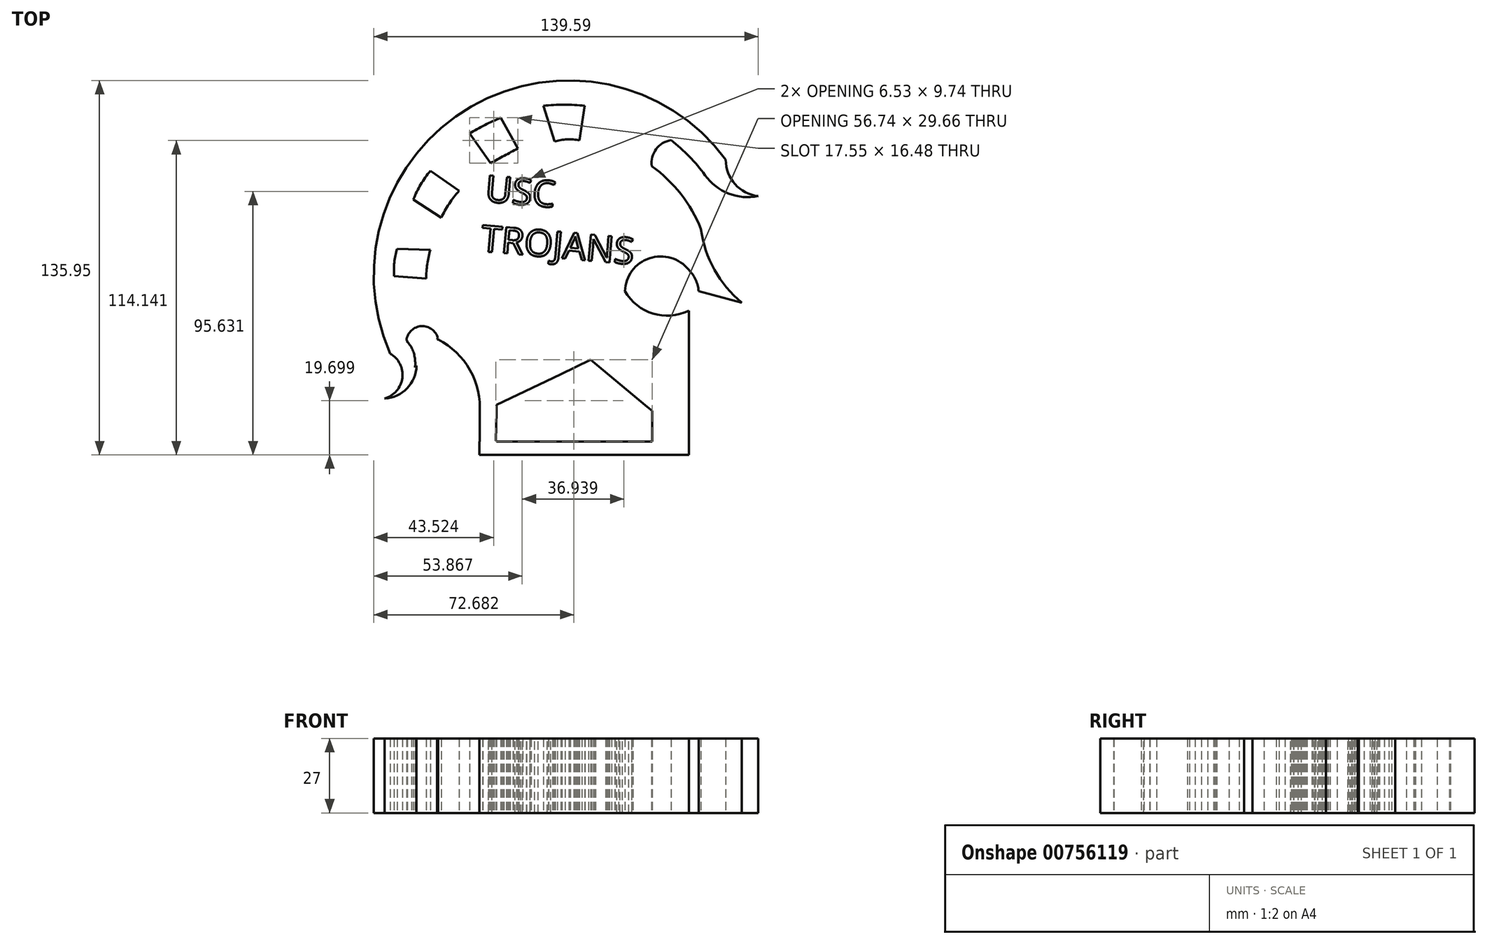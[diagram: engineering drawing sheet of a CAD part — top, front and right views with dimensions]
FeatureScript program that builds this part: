
annotation { "Feature Type Name" : "Feature", "Feature Type Description" : "" }
export const myFeature = defineFeature(function(context is Context, id is Id, definition is map)
    precondition{}
    {
        {
            var Q0;
            Q0=qCreatedBy(makeId("Top.planeOp"),FACE);
            var sketch = newSketch(context, id + "F0", { "sketchPlane" : qUnion([Q0])});
            skLineSegment(sketch, "E0", {"start": v(13.07, -40.22) * mm, "end": v(48.67, -69.88) * mm});
            skLineSegment(sketch, "E1", {"start": v(48.67, -69.88) * mm, "end": v(48.67, -22.42) * mm});
            skArc(sketch, "E2", {"start": v(25.5, -15.31) * mm, "mid": v(35.68, -23.46) * mm, "end": v(48.67, -22.42) * mm});
            skArc(sketch, "E3", {"start": v(48.67, -7.6) * mm, "mid": v(34.4, -3.36) * mm, "end": v(25.5, -15.31) * mm});
            skArc(sketch, "E4", {"start": v(52.23, -15.3) * mm, "mid": v(51.15, -11.12) * mm, "end": v(48.67, -7.6) * mm});
            skLineSegment(sketch, "E5", {"start": v(52.23, -15.3) * mm, "end": v(67.95, -19.46) * mm});
            skLineSegment(sketch, "E6", {"start": v(13.07, -40.22) * mm, "end": v(-27.27, -59.8) * mm});
            skArc(sketch, "E7", {"start": v(-27.27, -59.8) * mm, "mid": v(-30.74, -44) * mm, "end": v(-42.4, -32.8) * mm});
            skArc(sketch, "E8", {"start": v(53.1, 7.23) * mm, "mid": v(57.98, -7.53) * mm, "end": v(67.95, -19.46) * mm});
            skArc(sketch, "E9", {"start": v(53.1, 7.23) * mm, "mid": v(-15, 35.76) * mm, "end": v(-42.4, -32.8) * mm});
            skLineSegment(sketch, "E10", {"start": v(-53.77, -33.5) * mm, "end": v(-59.73, -38) * mm});
            skArc(sketch, "E11", {"start": v(-61.7, -54.3) * mm, "mid": v(-55.32, -46.8) * mm, "end": v(-59.73, -38) * mm});
            skArc(sketch, "E12", {"start": v(-61.7, -54.3) * mm, "mid": v(-50.96, -46.48) * mm, "end": v(-53.77, -33.5) * mm});
            skArc(sketch, "E13", {"start": v(54.63, 26.77) * mm, "mid": v(-26.23, 44.58) * mm, "end": v(-53.77, -33.5) * mm});
            skLineSegment(sketch, "E14", {"start": v(54.63, 26.77) * mm, "end": v(62.1, 32.38) * mm});
            skArc(sketch, "E15", {"start": v(62.1, 32.38) * mm, "mid": v(-30.31, 51.7) * mm, "end": v(-59.73, -38) * mm});
            skLineSegment(sketch, "E16", {"start": v(29.4, 33.69) * mm, "end": v(36.67, 43.31) * mm});
            skLineSegment(sketch, "E17", {"start": v(36.67, 43.31) * mm, "end": v(42.22, 39.5) * mm});
            skArc(sketch, "E18", {"start": v(42.22, 39.5) * mm, "mid": v(36.8, 36.22) * mm, "end": v(35.21, 30.08) * mm});
            skArc(sketch, "E19", {"start": v(62.1, 32.38) * mm, "mid": v(65.5, 23.54) * mm, "end": v(73.9, 19.19) * mm});
            skArc(sketch, "E20", {"start": v(54.63, 26.77) * mm, "mid": v(63.15, 20.14) * mm, "end": v(73.9, 19.19) * mm});
            skArc(sketch, "E21", {"start": v(36.67, 43.31) * mm, "mid": v(-36.33, 37.62) * mm, "end": v(-53.77, -33.5) * mm});
            skArc(sketch, "E22", {"start": v(29.4, 33.69) * mm, "mid": v(-29.9, 25.72) * mm, "end": v(-42.4, -32.8) * mm});
            skLineSegment(sketch, "E23", {"start": v(-53.77, -33.5) * mm, "end": v(-42.4, -32.8) * mm});
            skPoint(sketch, "E24.oppositeSnap0", {"position": v(-29.9, 25.72) * mm});
            skLineSegment(sketch, "E24.bottom", {"start": v(48.67, -69.88) * mm, "end": v(-29.9, -69.88) * mm});
            skLineSegment(sketch, "E24.top", {"start": v(48.67, -74.75) * mm, "end": v(-29.9, -74.75) * mm});
            skLineSegment(sketch, "E24.left", {"start": v(48.67, -69.88) * mm, "end": v(48.67, -74.75) * mm});
            skLineSegment(sketch, "E24.right", {"start": v(-29.9, -69.88) * mm, "end": v(-29.9, -74.75) * mm});
            skLineSegment(sketch, "E25.bottom", {"start": v(-21.13, -56.82) * mm, "end": v(-26.98, -56.82) * mm});
            skLineSegment(sketch, "E25.top", {"start": v(-21.13, -69.88) * mm, "end": v(-26.98, -69.88) * mm});
            skLineSegment(sketch, "E25.left", {"start": v(-21.13, -56.82) * mm, "end": v(-21.13, -69.88) * mm});
            skLineSegment(sketch, "E26", {"start": v(-27.27, -59.8) * mm, "end": v(-27.27, -69.88) * mm});
            skLineSegment(sketch, "E27", {"start": v(44.52, -69.88) * mm, "end": v(48.67, -69.88) * mm});
            skLineSegment(sketch, "E28", {"start": v(35.36, -58.8) * mm, "end": v(35.36, -69.88) * mm});
            skLineSegment(sketch, "E29", {"start": v(35.36, -69.88) * mm, "end": v(48.67, -69.88) * mm});
            skSolve(sketch);
        }
        {
            var Q0;
            Q0=qCreatedBy(makeId("Top.planeOp"),FACE);
            var sketch = newSketch(context, id + "F1", { "sketchPlane" : qUnion([Q0])});
            skArc(sketch, "E30", {"start": v(-42.4, -32.38) * mm, "mid": v(-48.38, -28.02) * mm, "end": v(-53.8, -33.06) * mm});
            skLineSegment(sketch, "E31", {"start": v(-42.4, -32.38) * mm, "end": v(-50.72, -43.05) * mm});
            skArc(sketch, "E32", {"start": v(-50.72, -43.05) * mm, "mid": v(-51.19, -37.73) * mm, "end": v(-53.8, -33.06) * mm});
            skLineSegment(sketch, "E33", {"start": v(-23.23, 31.15) * mm, "end": v(-30.94, 41.94) * mm});
            skArc(sketch, "E34", {"start": v(-19.56, 47.63) * mm, "mid": v(-25.37, 45.02) * mm, "end": v(-30.94, 41.94) * mm});
            skLineSegment(sketch, "E35", {"start": v(-19.56, 47.63) * mm, "end": v(-13.4, 36.49) * mm});
            skArc(sketch, "E36", {"start": v(-13.4, 36.49) * mm, "mid": v(-18.33, 33.85) * mm, "end": v(-23.23, 31.15) * mm});
            skLineSegment(sketch, "E37", {"start": v(-41.24, 11.35) * mm, "end": v(-51.3, 18) * mm});
            skArc(sketch, "E38", {"start": v(-45.13, 28.38) * mm, "mid": v(-48.63, 23.44) * mm, "end": v(-51.3, 18) * mm});
            skLineSegment(sketch, "E39", {"start": v(-45.13, 28.38) * mm, "end": v(-34.75, 21.09) * mm});
            skArc(sketch, "E40", {"start": v(-34.75, 21.09) * mm, "mid": v(-38.32, 16.44) * mm, "end": v(-41.24, 11.35) * mm});
            skLineSegment(sketch, "E41", {"start": v(-46.65, -10.77) * mm, "end": v(-58.27, -9.82) * mm});
            skArc(sketch, "E42", {"start": v(-57.22, 0) * mm, "mid": v(-58.22, -4.86) * mm, "end": v(-58.27, -9.82) * mm});
            skLineSegment(sketch, "E43", {"start": v(-57.22, 0) * mm, "end": v(-45.16, -0.32) * mm});
            skArc(sketch, "E44", {"start": v(-45.16, -0.32) * mm, "mid": v(-46.28, -5.5) * mm, "end": v(-46.65, -10.77) * mm});
            skLineSegment(sketch, "E45", {"start": v(0, 39.09) * mm, "end": v(-4.15, 52) * mm});
            skArc(sketch, "E46", {"start": v(10.94, 52) * mm, "mid": v(3.4, 52.4) * mm, "end": v(-4.15, 52) * mm});
            skLineSegment(sketch, "E47", {"start": v(10.94, 52) * mm, "end": v(9, 39.48) * mm});
            skArc(sketch, "E48", {"start": v(9, 39.48) * mm, "mid": v(4.48, 39.78) * mm, "end": v(0, 39.09) * mm});
            skText(sketch, "E49", { "text": "USC \nTROJANS", "fontName": "NotoSans-Regular.ttf"});
            skLineSegment(sketch, "E50.bottom", {"start": v(-27.29, -69.86) * mm, "end": v(-29.96, -69.86) * mm});
            skLineSegment(sketch, "E50.top", {"start": v(-27.29, -74.76) * mm, "end": v(-29.96, -74.76) * mm});
            skLineSegment(sketch, "E50.left", {"start": v(-27.29, -69.86) * mm, "end": v(-27.29, -74.76) * mm});
            skLineSegment(sketch, "E50.right", {"start": v(-29.96, -69.86) * mm, "end": v(-29.96, -74.76) * mm});
            skLineSegment(sketch, "E51", {"start": v(-21.08, -56.6) * mm, "end": v(13.05, -40.32) * mm});
            skLineSegment(sketch, "E52", {"start": v(13.05, -40.32) * mm, "end": v(35.35, -58.77) * mm});
            skLineSegment(sketch, "E53", {"start": v(35.35, -58.77) * mm, "end": v(35.35, -69.72) * mm});
            skLineSegment(sketch, "E54", {"start": v(35.35, -69.72) * mm, "end": v(-21.38, -69.72) * mm});
            skLineSegment(sketch, "E55", {"start": v(-21.38, -69.72) * mm, "end": v(-21.08, -56.6) * mm});
            const initialGuessF1  = {"E49": [-0.0255, 0.0173, 0.9962, -0.08716, 0.0096]};
            skSetInitialGuess(sketch, initialGuessF1);
            skSolve(sketch);
        }
        {
            var Q0;
            Q0 = qSketchRegion(id + "F0", true);
            extrude(context, id + "F2", {"entities" : qUnion([Q0]), "depth" : 27 * mm, "offsetDistance" : 25 * mm});
        }
        {
            var Q0;
            Q0 = qSketchRegion(id + "F1", true);
            extrude(context, id + "F3", {"entities" : qUnion([Q0]), "operationType" : NewBodyOperationType.REMOVE, "depth" : 38.1 * mm, "offsetDistance" : 25 * mm});
        }
    });
